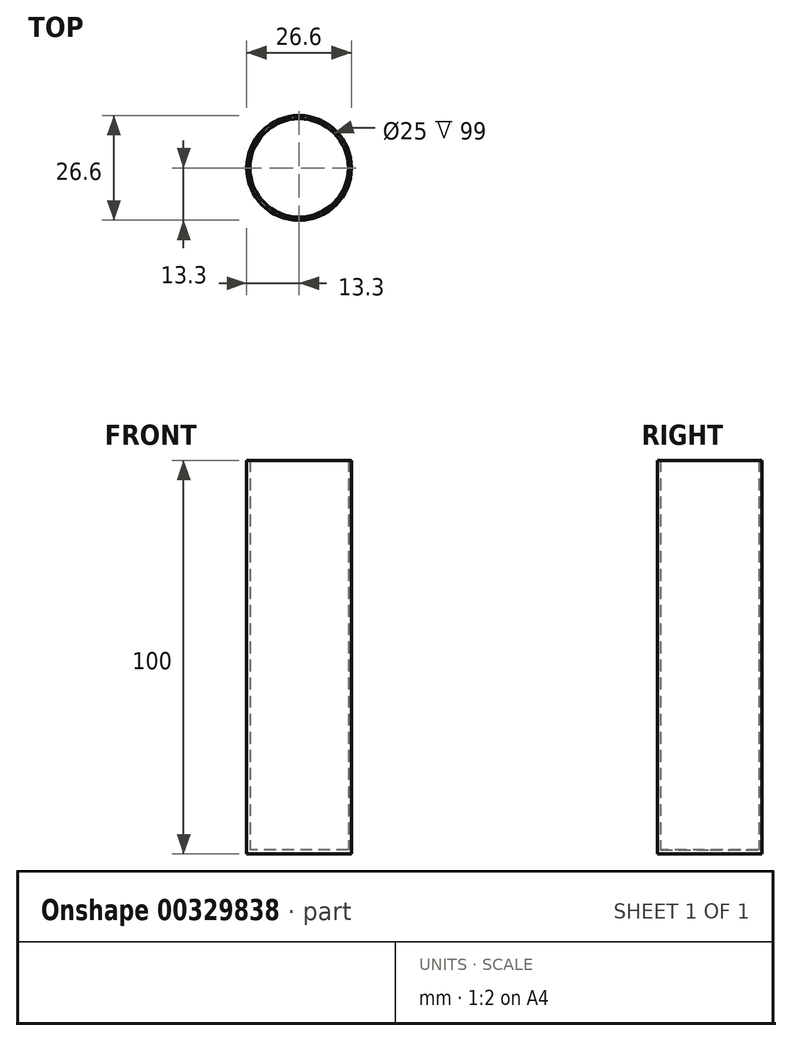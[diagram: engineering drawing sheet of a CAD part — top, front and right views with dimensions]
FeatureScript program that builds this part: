
annotation { "Feature Type Name" : "Feature", "Feature Type Description" : "" }
export const myFeature = defineFeature(function(context is Context, id is Id, definition is map)
    precondition{}
    {
        {
            var Q0;
            Q0=qCreatedBy(makeId("Top.planeOp"),FACE);
            var sketch = newSketch(context, id + "F0", { "sketchPlane" : qUnion([Q0])});
            skCircle(sketch, "E0", {"center": v(0, 0) * mm, "radius": 12.5 * mm});
            skCircle(sketch, "E1", {"center": v(0, 0) * mm, "radius": 13.3 * mm});
            skSolve(sketch);
        }
        {
            var Q0;
            Q0=makeQuery(id+"F0.imprint","IMPRINT",FACE,{"disambiguationData":[TD([[makeQuery(id+"F0.imprint","IMPRINT",EDGE,{"derivedFrom":sQuery(id+"F0.wireOp",EDGE,"E0")}),1.0]])]});
            var Q1;
            Q1=makeQuery(id+"F0.imprint","IMPRINT",FACE,{"disambiguationData":[TD([[makeQuery(id+"F0.imprint","IMPRINT",EDGE,{"derivedFrom":sQuery(id+"F0.wireOp",EDGE,"E0")}),-1.0]])]});
            extrude(context, id + "F1", {"entities" : qUnion([Q0, Q1]), "depth" : 1 * mm, "offsetDistance" : 25 * mm});
        }
        {
            var Q0;
            Q0=makeQuery(id+"F0.imprint","IMPRINT",FACE,{"disambiguationData":[TD([[makeQuery(id+"F0.imprint","IMPRINT",EDGE,{"derivedFrom":sQuery(id+"F0.wireOp",EDGE,"E0")}),-1.0]])]});
            extrude(context, id + "F2", {"entities" : qUnion([Q0]), "operationType" : NewBodyOperationType.ADD, "depth" : 100 * mm, "offsetDistance" : 25 * mm});
        }
    });
